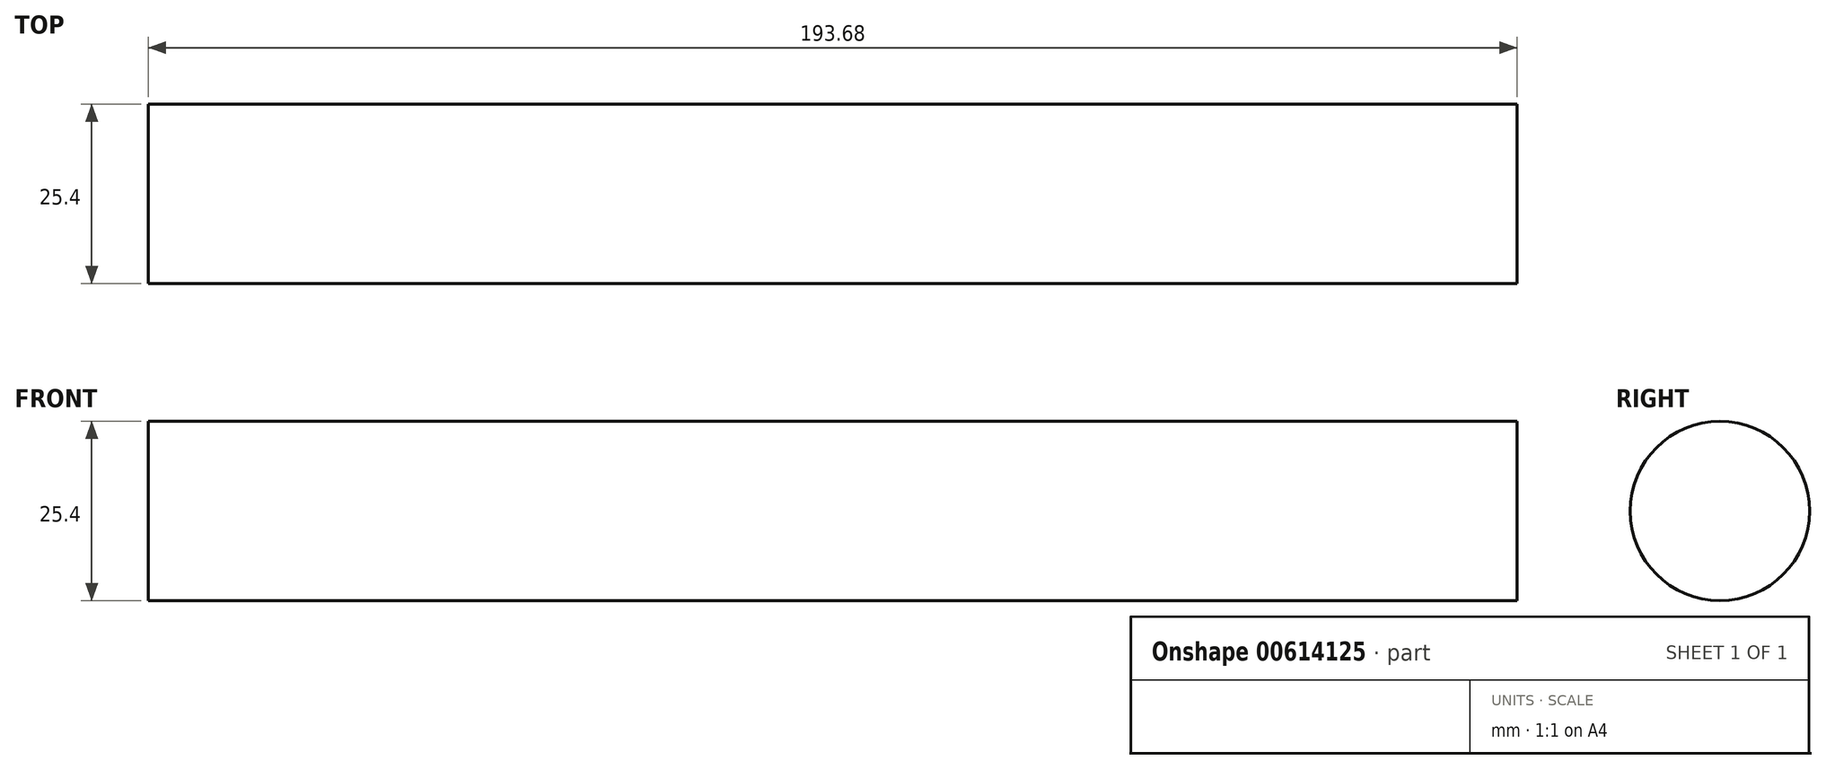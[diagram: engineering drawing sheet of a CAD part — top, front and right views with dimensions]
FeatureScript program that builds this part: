
annotation { "Feature Type Name" : "Feature", "Feature Type Description" : "" }
export const myFeature = defineFeature(function(context is Context, id is Id, definition is map)
    precondition{}
    {
        {
            var Q0;
            Q0=qCreatedBy(makeId("Right.planeOp"),FACE);
            var sketch = newSketch(context, id + "F0", { "sketchPlane" : qUnion([Q0])});
            skCircle(sketch, "E0", {"center": v(0, 0) * mm, "radius": 12.7 * mm});
            skSolve(sketch);
        }
        {
            var Q0;
            Q0 = qSketchRegion(id + "F0", true);
            extrude(context, id + "F1", {"entities" : qUnion([Q0]), "depth" : 193.67 * mm, "offsetDistance" : 25.4 * mm});
        }
    });
